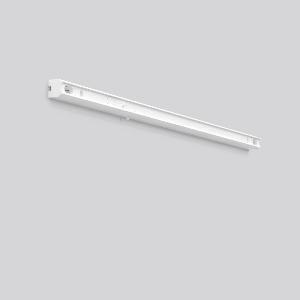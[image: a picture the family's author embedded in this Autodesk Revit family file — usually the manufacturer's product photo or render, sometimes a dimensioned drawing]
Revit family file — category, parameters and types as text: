
# Revit family: alu-stableuchten_41521_002_101a
name_source: partatom
category: Lighting Fixtures
units: mm (PartAtom-declared; Revit-internal decimal feet)

## family parameters
Cut with Voids When Loaded = No
Host = Face
Light Source = No
Part Type = Normal
Room Calculation Point = No
Round Connector Dimension = Use Diameter
Shared = No

## types (1)
- ALU-Stableuchten (1 x LED L S14S, 1000 lm, 16 W, 2700)
    Apparent Load = 16 VA
    CIE Flux Codes = 34 61 82 75 81
    Color Rendering = 80
    Color Temperature = 2700
    Default Elevation = 1800 mm
    Description = Series: Aluminium striplights
Aluminium striplight for linear lamps. Base: aluminium extrusion profile, powder-coated. End caps: plastic. With push button switch. Lamp contacts disconnection during lamp replacement. Light source must be ordered separately. 
Colour: white
Length: 1000 mm
Width: 35 mm
Height: 58 mm
Lamp: L-DE
Number of lamps: 1
Wattage: 120 W
Socket: S14s
System power: 30 W
Rated luminous flux: 1100 lm
Luminous efficiency: 37 lm/W
Control gear: Converter not necessary
Protection class: I
Type of protection: IP 40
    Height = 58 mm
    Lamp = 1 x LED L S14S
    Lamp Light Flux = 1000 lm
    Lamp Power = 16 W
    Lamp count = 1
    Length = 1000 mm  [stored 3.28084 ft]
    Lifetime = 25000 h
    Luminous efficacy = 51 lm/W
    Manufacturer = RZB
    ModVariant = No
    Model = 41521.002
    Mounting Place = Ceiling, Wall
    Mounting Type = Surface mounted
    Number of Poles = 1
    OnlyDefault = Yes
    Power Factor = 1
    Product Name = ALU-Stableuchten
    Product group = Surface mounted ceiling and wall luminaires
    ProductGroupID = 305
    Protection Class = Protection class I
    Protection Degree = IP 40
    RLX_Detail_Level = 1
    RLX_Emergency_Light_Flux = 0 lm
    RLX_Emergency_Type = 0
    RLX_Emergency_Type_DB = No
    RlxData = <blob elided: 15101 chars, md5=0007ac89>
    Socket = S14s
    Standby Power = 0 W
    System Light Flux = 813 lm
    System Power = 16 W
    Type Comments = Product without accessories
    Type Image = 41521.002.jpg
    URL = http://relux.com
    VarID = ---
    Voltage = 230 V
    Voltage Range = 220-240 V
    Weight = 0.00 kg
    Width = 35 mm

note: [stored X ft] marks values corroborated as IEEE doubles in the binary element streams (Revit-internal decimal feet)

## geometry (parser evidence)
native form markers: Sweep x13
no freeform markers — native parametric forms only
